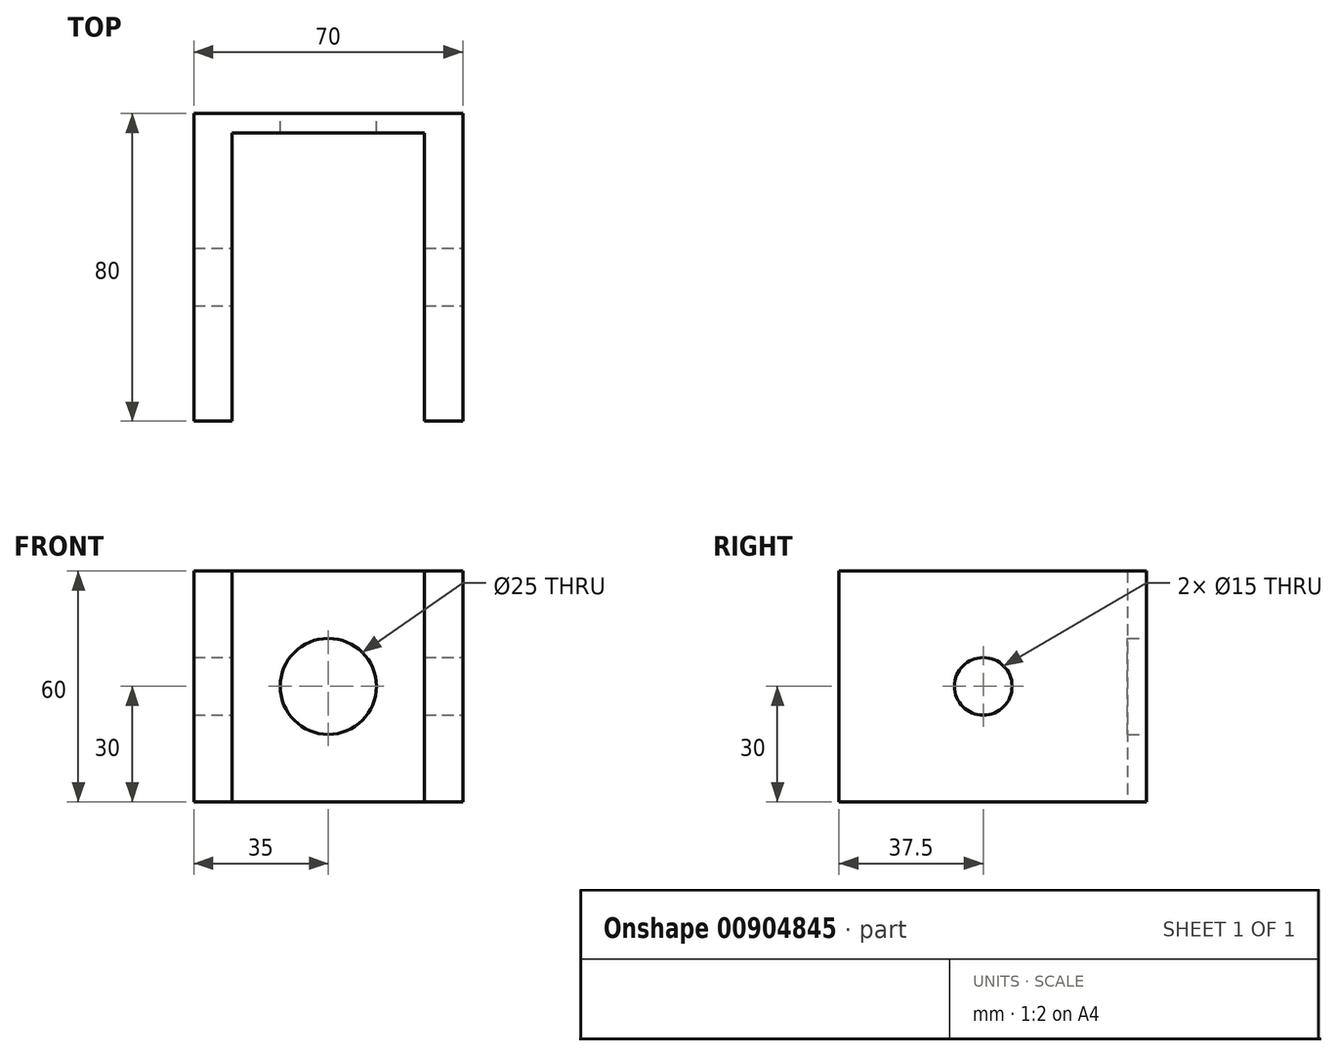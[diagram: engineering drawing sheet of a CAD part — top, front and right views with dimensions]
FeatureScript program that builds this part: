
annotation { "Feature Type Name" : "Feature", "Feature Type Description" : "" }
export const myFeature = defineFeature(function(context is Context, id is Id, definition is map)
    precondition{}
    {
        {
            var Q0;
            Q0=qCreatedBy(makeId("Front.planeOp"),FACE);
            var sketch = newSketch(context, id + "F0", { "sketchPlane" : qUnion([Q0])});
            skLineSegment(sketch, "E0.bottom", {"start": v(35, 30) * mm, "end": v(-35, 30) * mm});
            skLineSegment(sketch, "E0.top", {"start": v(35, -30) * mm, "end": v(-35, -30) * mm});
            skLineSegment(sketch, "E0.left", {"start": v(35, 30) * mm, "end": v(35, -30) * mm});
            skLineSegment(sketch, "E0.right", {"start": v(-35, 30) * mm, "end": v(-35, -30) * mm});
            skPoint(sketch, "E0.middle", {"position": v(0, 0) * mm});
            skCircle(sketch, "E1", {"center": v(0, 0) * mm, "radius": 12.5 * mm});
            skSolve(sketch);
        }
        {
            var Q0;
            Q0=makeQuery(id+"F0.imprint","IMPRINT",FACE,{"disambiguationData":[TD([[makeQuery(id+"F0.imprint","IMPRINT",EDGE,{"derivedFrom":sQuery(id+"F0.wireOp",EDGE,"E0.bottom")}),1.0]])]});
            extrude(context, id + "F1", {"entities" : qUnion([Q0]), "depth" : 5 * mm, "offsetDistance" : 25 * mm});
        }
        {
            var Q0;
            Q0=makeQuery(id+"F1.opExtrude","CAP_FACE",FACE,{"disambiguationData":[OSD([sQuery(id+"F0.wireOp",EDGE,"E0.bottom"),sQuery(id+"F0.wireOp",EDGE,"E0.top"),sQuery(id+"F0.wireOp",EDGE,"E0.left"),sQuery(id+"F0.wireOp",EDGE,"E0.right"),sQuery(id+"F0.wireOp",EDGE,"E1")])],"isStart":false});
            var sketch = newSketch(context, id + "F2", { "sketchPlane" : qUnion([Q0])});
            skLineSegment(sketch, "E2.bottom", {"start": v(-35, 30) * mm, "end": v(-25, 30) * mm});
            skLineSegment(sketch, "E2.top", {"start": v(-35, -30) * mm, "end": v(-25, -30) * mm});
            skLineSegment(sketch, "E2.left", {"start": v(-35, 30) * mm, "end": v(-35, -30) * mm});
            skLineSegment(sketch, "E2.right", {"start": v(-25, 30) * mm, "end": v(-25, -30) * mm});
            skLineSegment(sketch, "E3.bottom", {"start": v(35, 30) * mm, "end": v(25, 30) * mm});
            skLineSegment(sketch, "E3.top", {"start": v(35, -30) * mm, "end": v(25, -30) * mm});
            skLineSegment(sketch, "E3.left", {"start": v(35, 30) * mm, "end": v(35, -30) * mm});
            skLineSegment(sketch, "E3.right", {"start": v(25, 30) * mm, "end": v(25, -30) * mm});
            skSolve(sketch);
        }
        {
            var Q0;
            Q0 = qSketchRegion(id + "F2", true);
            extrude(context, id + "F3", {"entities" : qUnion([Q0]), "operationType" : NewBodyOperationType.ADD, "depth" : 75 * mm, "offsetDistance" : 25 * mm});
        }
        {
            var Q0;
            Q0=makeQuery(id+"F3.boolean.opBoolean","MERGE",FACE,{"derivedFrom":[makeQuery(id+"F1.opExtrude","SWEPT_FACE",FACE,{"disambiguationData":[OSD([sQuery(id+"F0.wireOp",EDGE,"E0.left")])]}),makeQuery(id+"F3.opExtrude","SWEPT_FACE",FACE,{"disambiguationData":[OSD([sQuery(id+"F2.wireOp",EDGE,"E3.left")])]})]});
            var sketch = newSketch(context, id + "F4", { "sketchPlane" : qUnion([Q0])});
            skPoint(sketch, "E4", {"position": v(-42.5, 0) * mm});
            skCircle(sketch, "E5", {"center": v(-42.5, 0) * mm, "radius": 7.5 * mm});
            skSolve(sketch);
        }
        {
            var Q0;
            Q0=makeQuery(id+"F4.imprint","IMPRINT",FACE,{"disambiguationData":[TD([[makeQuery(id+"F4.imprint","IMPRINT",EDGE,{"derivedFrom":sQuery(id+"F4.wireOp",EDGE,"E5")}),1.0]])]});
            extrude(context, id + "F5", {"entities" : qUnion([Q0]), "operationType" : NewBodyOperationType.REMOVE, "endBound" : BoundingType.THROUGH_ALL, "oppositeDirection" : true, "depth" : 25 * mm, "offsetDistance" : 25 * mm});
        }
    });
